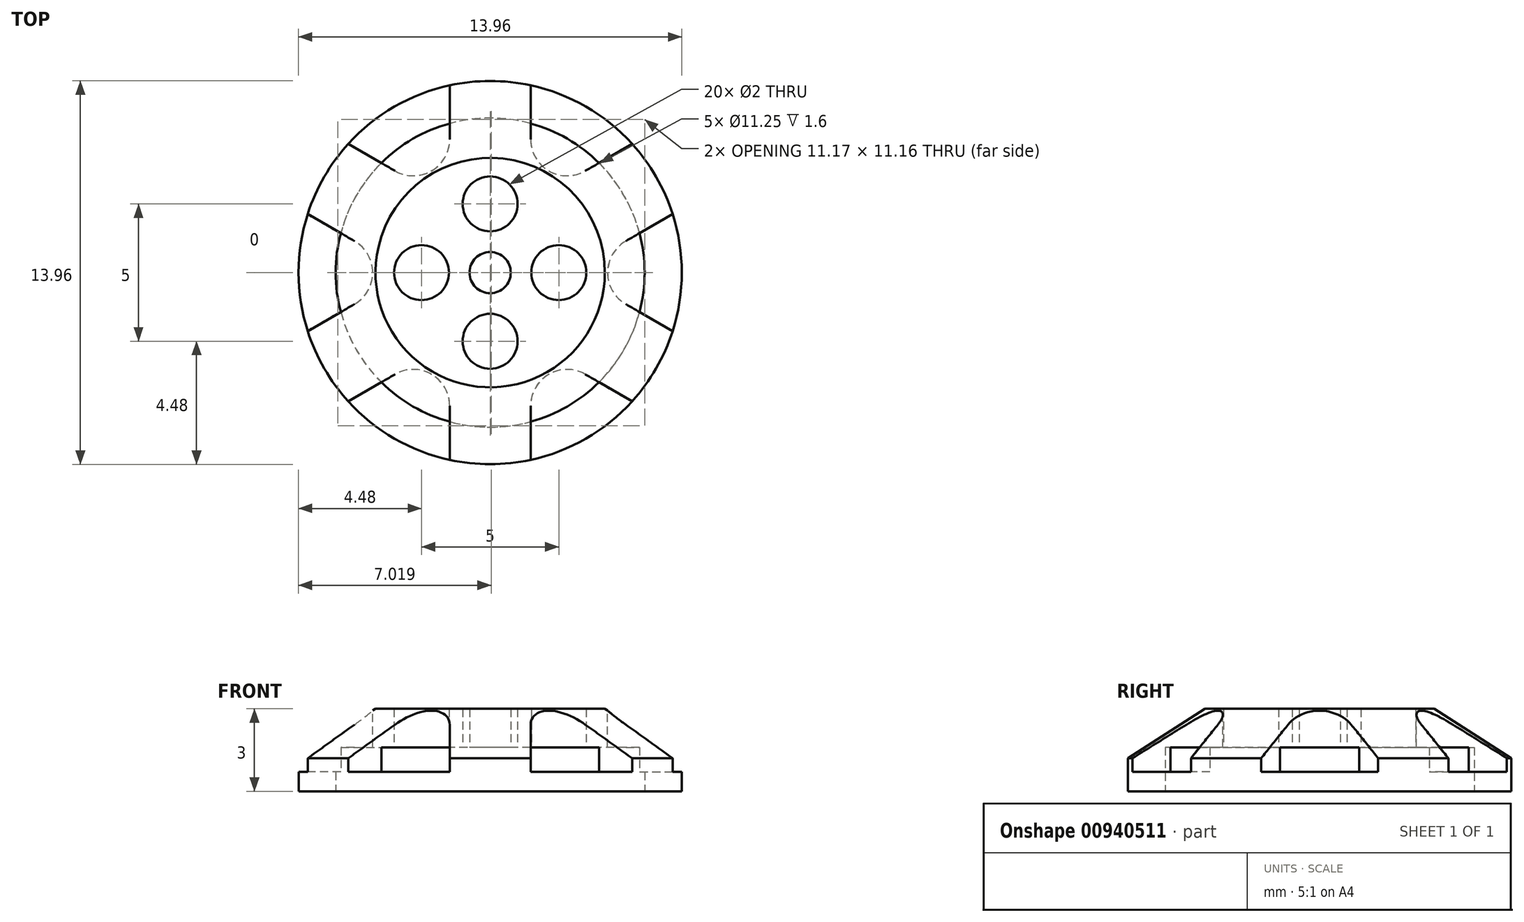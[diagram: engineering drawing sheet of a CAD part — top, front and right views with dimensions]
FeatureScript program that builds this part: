
annotation { "Feature Type Name" : "Feature", "Feature Type Description" : "" }
export const myFeature = defineFeature(function(context is Context, id is Id, definition is map)
    precondition{}
    {
        {
            var Q0;
            Q0=qCreatedBy(makeId("Top.planeOp"),FACE);
            var sketch = newSketch(context, id + "F0", { "sketchPlane" : qUnion([Q0])});
            skCircle(sketch, "E0", {"center": v(0, 0) * mm, "radius": 6.97 * mm});
            skCircle(sketch, "E1", {"center": v(0, 2.5) * mm, "radius": 1 * mm});
            skCircle(sketch, "E2.0", {"center": v(0, 0) * mm, "radius": 5.62 * mm});
            skCircle(sketch, "E3", {"center": v(0, 0) * mm, "radius": 0.75 * mm});
            skCircle(sketch, "E4.1.0", {"center": v(-2.5, 0) * mm, "radius": 1 * mm});
            skCircle(sketch, "E4.2.0", {"center": v(0, -2.5) * mm, "radius": 1 * mm});
            skCircle(sketch, "E4.3.0", {"center": v(2.5, 0) * mm, "radius": 1 * mm});
            skSolve(sketch);
        }
        {
            var Q0;
            Q0=makeQuery(id+"F0.imprint","IMPRINT",FACE,{"disambiguationData":[TD([[makeQuery(id+"F0.imprint","IMPRINT",EDGE,{"derivedFrom":sQuery(id+"F0.wireOp",EDGE,"E0")}),1.0]])]});
            var Q1;
            Q1=makeQuery(id+"F0.imprint","IMPRINT",FACE,{"disambiguationData":[TD([[makeQuery(id+"F0.imprint","IMPRINT",EDGE,{"derivedFrom":sQuery(id+"F0.wireOp",EDGE,"E1")}),-1.0]])]});
            extrude(context, id + "F1", {"entities" : qUnion([Q0, Q1]), "depth" : 3 * mm, "offsetDistance" : 25 * mm});
        }
        {
            var Q0;
            Q0=makeQuery(id+"F1.opExtrude","CAP_EDGE",EDGE,{"disambiguationData":[OSD([sQuery(id+"F0.wireOp",EDGE,"E0")])],"isStart":false});
            chamfer(context, id + "F2", {"entities" : qUnion([Q0]), "chamferType" : ChamferType.TWO_OFFSETS, "width1" : 2.8 * mm, "oppositeDirection" : false, "width2" : (3 - 1.2) * mm, "tangentPropagation" : true});
        }
        {
            var Q0;
            Q0=makeQuery(id+"F1.opExtrude","CAP_FACE",FACE,{"disambiguationData":[OSD([sQuery(id+"F0.wireOp",EDGE,"E0"),sQuery(id+"F0.wireOp",EDGE,"E1"),sQuery(id+"F0.wireOp",EDGE,"E3"),sQuery(id+"F0.wireOp",EDGE,"E4.1.0"),sQuery(id+"F0.wireOp",EDGE,"E4.2.0"),sQuery(id+"F0.wireOp",EDGE,"E4.3.0")])],"isStart":false});
            var sketch = newSketch(context, id + "F3", { "sketchPlane" : qUnion([Q0])});
            skPoint(sketch, "E5", {"position": v(0, 0) * mm});
            skLineSegment(sketch, "E6.left", {"start": v(-1.48, 6.82) * mm, "end": v(-1.48, 3.9) * mm});
            skLineSegment(sketch, "E6.right", {"start": v(1.48, 6.82) * mm, "end": v(1.48, 3.9) * mm});
            skArc(sketch, "E7", {"start": v(-1.48, 3.9) * mm, "mid": v(0, 4.17) * mm, "end": v(1.48, 3.9) * mm, "construction": true});
            skPoint(sketch, "E8", {"position": v(0, 4.17) * mm});
            skLineSegment(sketch, "E9.1.0", {"start": v(-6.64, 2.13) * mm, "end": v(-4.12, 0.68) * mm});
            skLineSegment(sketch, "E9.1.1", {"start": v(-5.17, 4.69) * mm, "end": v(-2.64, 3.23) * mm});
            skLineSegment(sketch, "E9.2.0", {"start": v(-5.17, -4.69) * mm, "end": v(-2.64, -3.23) * mm});
            skLineSegment(sketch, "E9.2.1", {"start": v(-6.64, -2.13) * mm, "end": v(-4.12, -0.68) * mm});
            skLineSegment(sketch, "E9.3.0", {"start": v(1.47, -6.82) * mm, "end": v(1.47, -3.9) * mm});
            skLineSegment(sketch, "E9.3.1", {"start": v(-1.48, -6.82) * mm, "end": v(-1.48, -3.9) * mm});
            skLineSegment(sketch, "E9.4.0", {"start": v(6.64, -2.13) * mm, "end": v(4.12, -0.68) * mm});
            skLineSegment(sketch, "E9.4.1", {"start": v(5.17, -4.69) * mm, "end": v(2.64, -3.23) * mm});
            skLineSegment(sketch, "E9.5.0", {"start": v(5.17, 4.69) * mm, "end": v(2.64, 3.23) * mm});
            skLineSegment(sketch, "E9.5.1", {"start": v(6.64, 2.13) * mm, "end": v(4.12, 0.68) * mm});
            skArc(sketch, "E10", {"start": v(-4.94, -1.15) * mm, "mid": v(-4.27, 0) * mm, "end": v(-4.94, 1.15) * mm});
            skArc(sketch, "E11", {"start": v(-6.64, -2.13) * mm, "mid": v(-6.97, 0) * mm, "end": v(-6.64, 2.13) * mm});
            skArc(sketch, "E12.1.0", {"start": v(-1.48, -4.85) * mm, "mid": v(-2.14, -3.7) * mm, "end": v(-3.46, -3.7) * mm});
            skArc(sketch, "E12.1.1", {"start": v(-1.48, -6.82) * mm, "mid": v(-3.49, -6.04) * mm, "end": v(-5.17, -4.69) * mm});
            skArc(sketch, "E12.2.0", {"start": v(3.46, -3.7) * mm, "mid": v(2.14, -3.7) * mm, "end": v(1.47, -4.85) * mm});
            skArc(sketch, "E12.2.1", {"start": v(5.17, -4.69) * mm, "mid": v(3.49, -6.04) * mm, "end": v(1.47, -6.82) * mm});
            skArc(sketch, "E12.3.0", {"start": v(4.94, 1.15) * mm, "mid": v(4.27, 0) * mm, "end": v(4.94, -1.15) * mm});
            skArc(sketch, "E12.3.1", {"start": v(6.64, 2.13) * mm, "mid": v(6.98, 0) * mm, "end": v(6.64, -2.13) * mm});
            skArc(sketch, "E12.4.0", {"start": v(1.48, 4.85) * mm, "mid": v(2.14, 3.7) * mm, "end": v(3.46, 3.7) * mm});
            skArc(sketch, "E12.4.1", {"start": v(1.48, 6.82) * mm, "mid": v(3.49, 6.04) * mm, "end": v(5.17, 4.69) * mm});
            skArc(sketch, "E12.5.0", {"start": v(-3.46, 3.7) * mm, "mid": v(-2.14, 3.7) * mm, "end": v(-1.48, 4.85) * mm});
            skArc(sketch, "E12.5.1", {"start": v(-5.17, 4.69) * mm, "mid": v(-3.49, 6.04) * mm, "end": v(-1.47, 6.82) * mm});
            skSolve(sketch);
        }
        {
            var Q0;
            {var subQ2=sQuery(id+"F3.wireOp",EDGE,"E12.5.0");Q0=makeQuery(id+"F3.imprint","IMPRINT",FACE,{"disambiguationData":[TD([[makeQuery(id+"F3.imprint","IMPRINT",EDGE,{"derivedFrom":subQ2}),1.0]])]});}
            var Q1;
            {var subQ2=sQuery(id+"F3.wireOp",EDGE,"E12.4.0");Q1=makeQuery(id+"F3.imprint","IMPRINT",FACE,{"disambiguationData":[TD([[makeQuery(id+"F3.imprint","IMPRINT",EDGE,{"derivedFrom":subQ2}),1.0]])]});}
            var Q2;
            {var subQ2=sQuery(id+"F3.wireOp",EDGE,"E12.3.0");Q2=makeQuery(id+"F3.imprint","IMPRINT",FACE,{"disambiguationData":[TD([[makeQuery(id+"F3.imprint","IMPRINT",EDGE,{"derivedFrom":subQ2}),1.0]])]});}
            var Q3;
            {var subQ2=sQuery(id+"F3.wireOp",EDGE,"E12.2.0");Q3=makeQuery(id+"F3.imprint","IMPRINT",FACE,{"disambiguationData":[TD([[makeQuery(id+"F3.imprint","IMPRINT",EDGE,{"derivedFrom":subQ2}),1.0]])]});}
            var Q4;
            {var subQ2=sQuery(id+"F3.wireOp",EDGE,"E12.1.0");Q4=makeQuery(id+"F3.imprint","IMPRINT",FACE,{"disambiguationData":[TD([[makeQuery(id+"F3.imprint","IMPRINT",EDGE,{"derivedFrom":subQ2}),1.0]])]});}
            var Q5;
            {var subQ2=sQuery(id+"F3.wireOp",EDGE,"E10");Q5=makeQuery(id+"F3.imprint","IMPRINT",FACE,{"disambiguationData":[TD([[makeQuery(id+"F3.imprint","IMPRINT",EDGE,{"derivedFrom":subQ2}),1.0]])]});}
            var Q6;
            Q6=makeQuery(id+"F1.opExtrude","CAP_FACE",FACE,{"disambiguationData":[OSD([sQuery(id+"F0.wireOp",EDGE,"E0"),sQuery(id+"F0.wireOp",EDGE,"E1"),sQuery(id+"F0.wireOp",EDGE,"E3"),sQuery(id+"F0.wireOp",EDGE,"E4.1.0"),sQuery(id+"F0.wireOp",EDGE,"E4.2.0"),sQuery(id+"F0.wireOp",EDGE,"E4.3.0")])],"isStart":true});
            extrude(context, id + "F4", {"entities" : qUnion([Q0, Q1, Q2, Q3, Q4, Q5]), "operationType" : NewBodyOperationType.REMOVE, "endBound" : BoundingType.UP_TO_SURFACE, "oppositeDirection" : true, "depth" : 25 * mm, "endBoundEntityFace" : qUnion([Q6]), "hasOffset" : true, "offsetDistance" : 0.7 * mm});
        }
        {
            var Q0;
            Q0=makeQuery(id+"F0.imprint","IMPRINT",FACE,{"disambiguationData":[TD([[makeQuery(id+"F0.imprint","IMPRINT",EDGE,{"derivedFrom":sQuery(id+"F0.wireOp",EDGE,"E1")}),-1.0]])]});
            var Q1;
            Q1=makeQuery(id+"F1.opExtrude","CAP_FACE",FACE,{"disambiguationData":[OSD([sQuery(id+"F0.wireOp",EDGE,"E0"),sQuery(id+"F0.wireOp",EDGE,"E1"),sQuery(id+"F0.wireOp",EDGE,"E3"),sQuery(id+"F0.wireOp",EDGE,"E4.1.0"),sQuery(id+"F0.wireOp",EDGE,"E4.2.0"),sQuery(id+"F0.wireOp",EDGE,"E4.3.0")])],"isStart":false});
            extrude(context, id + "F5", {"entities" : qUnion([Q0]), "operationType" : NewBodyOperationType.REMOVE, "endBound" : BoundingType.UP_TO_SURFACE, "depth" : 25 * mm, "endBoundEntityFace" : qUnion([Q1]), "hasOffset" : true, "offsetDistance" : 1.4 * mm});
        }
    });
